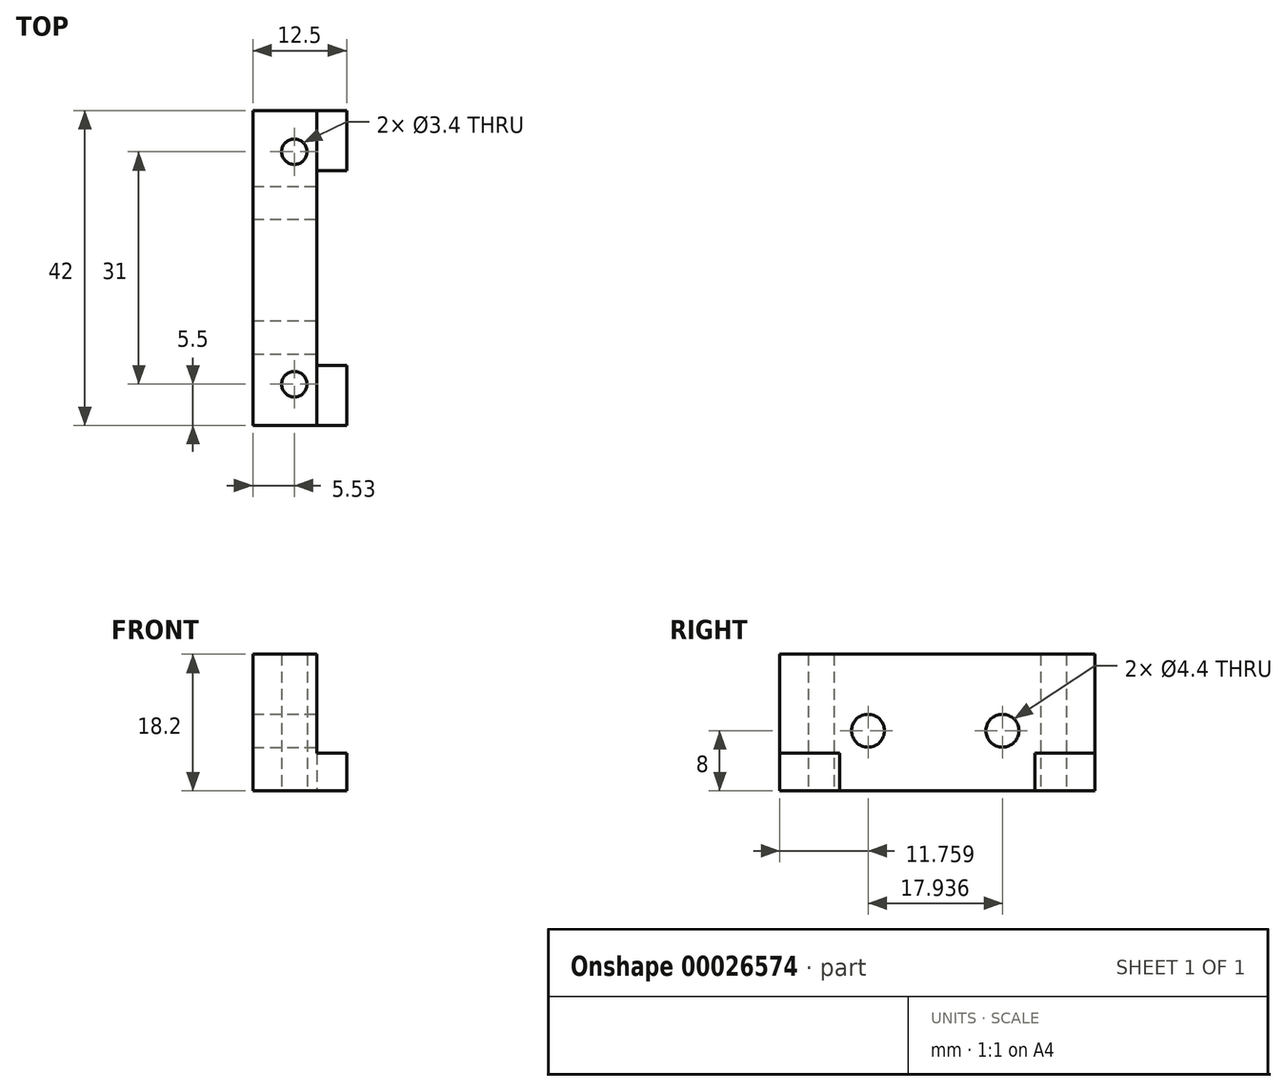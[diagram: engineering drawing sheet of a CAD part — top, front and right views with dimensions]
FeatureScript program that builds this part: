
annotation { "Feature Type Name" : "Feature", "Feature Type Description" : "" }
export const myFeature = defineFeature(function(context is Context, id is Id, definition is map)
    precondition{}
    {
        {
            var Q0;
            Q0=qCreatedBy(makeId("Front.planeOp"),FACE);
            var sketch = newSketch(context, id + "F0", { "sketchPlane" : qUnion([Q0])});
            skLineSegment(sketch, "E0", {"start": v(8.5, 18.2) * mm, "end": v(8.5, 5) * mm});
            skLineSegment(sketch, "E1", {"start": v(8.5, 5) * mm, "end": v(12.5, 5) * mm});
            skLineSegment(sketch, "E2", {"start": v(12.5, 5) * mm, "end": v(12.5, 0) * mm});
            skLineSegment(sketch, "E3", {"start": v(12.5, 0) * mm, "end": v(0, 0) * mm});
            skLineSegment(sketch, "E4", {"start": v(0, 0) * mm, "end": v(0, 18.2) * mm});
            skLineSegment(sketch, "E5", {"start": v(0, 18.2) * mm, "end": v(8.5, 18.2) * mm});
            skSolve(sketch);
        }
        {
            var Q0;
            Q0=qSketchRegion(id+"F0",true);
            extrude(context, id + "F1", {"entities" : qUnion([Q0]), "oppositeDirection" : true, "depth" : 42 * mm});
        }
        {
            var Q0;
            Q0=makeQuery(id+"F1.opExtrude","SWEPT_FACE",FACE,{"disambiguationData":[OSD([sQuery(id+"F0.wireOp",EDGE,"E3")])]});
            var sketch = newSketch(context, id + "F2", { "sketchPlane" : qUnion([Q0])});
            skCircle(sketch, "E6", {"center": v(5.53, -5.5) * mm, "radius": 1.7 * mm});
            skCircle(sketch, "E7", {"center": v(5.53, -36.5) * mm, "radius": 1.7 * mm});
            skCircle(sketch, "E8", {"center": v(21.03, -21) * mm, "radius": 11 * mm});
            skLineSegment(sketch, "E9", {"start": v(0, -21) * mm, "end": v(12.5, -21) * mm, "construction": true});
            skLineSegment(sketch, "E10.bottom", {"start": v(12.5, -8) * mm, "end": v(8.5, -8) * mm});
            skLineSegment(sketch, "E10.top", {"start": v(12.5, -34) * mm, "end": v(8.5, -34) * mm});
            skLineSegment(sketch, "E10.left", {"start": v(8.5, -8) * mm, "end": v(8.5, -34) * mm});
            skLineSegment(sketch, "E10.right", {"start": v(12.5, -8) * mm, "end": v(12.5, -34) * mm});
            skSolve(sketch);
        }
        {
            var Q0;
            Q0=qSketchRegion(id+"F2",true);
            extrude(context, id + "F3", {"entities" : qUnion([Q0]), "operationType" : NewBodyOperationType.REMOVE, "endBound" : BoundingType.THROUGH_ALL, "oppositeDirection" : true, "depth" : 25 * mm});
        }
        {
            var Q0;
            Q0=makeQuery(id+"F1.opExtrude","SWEPT_FACE",FACE,{"disambiguationData":[OSD([sQuery(id+"F0.wireOp",EDGE,"E0")])]});
            var sketch = newSketch(context, id + "F4", { "sketchPlane" : qUnion([Q0])});
            skCircle(sketch, "E11", {"center": v(11.76, 8) * mm, "radius": 2.2 * mm});
            skCircle(sketch, "E12", {"center": v(29.7, 8) * mm, "radius": 2.2 * mm});
            skPoint(sketch, "E13", {"position": v(7.56, 18.2) * mm});
            skPoint(sketch, "E14", {"position": v(33.9, 18.2) * mm});
            skLineSegment(sketch, "E15", {"start": v(7.56, 18.2) * mm, "end": v(7.56, 4.72) * mm, "construction": true});
            skLineSegment(sketch, "E16", {"start": v(33.9, 18.2) * mm, "end": v(33.9, 6.44) * mm, "construction": true});
            skSolve(sketch);
        }
        {
            var Q0;
            Q0=qSketchRegion(id+"F4",true);
            extrude(context, id + "F5", {"entities" : qUnion([Q0]), "operationType" : NewBodyOperationType.REMOVE, "oppositeDirection" : true, "depth" : 25 * mm});
        }
    });
